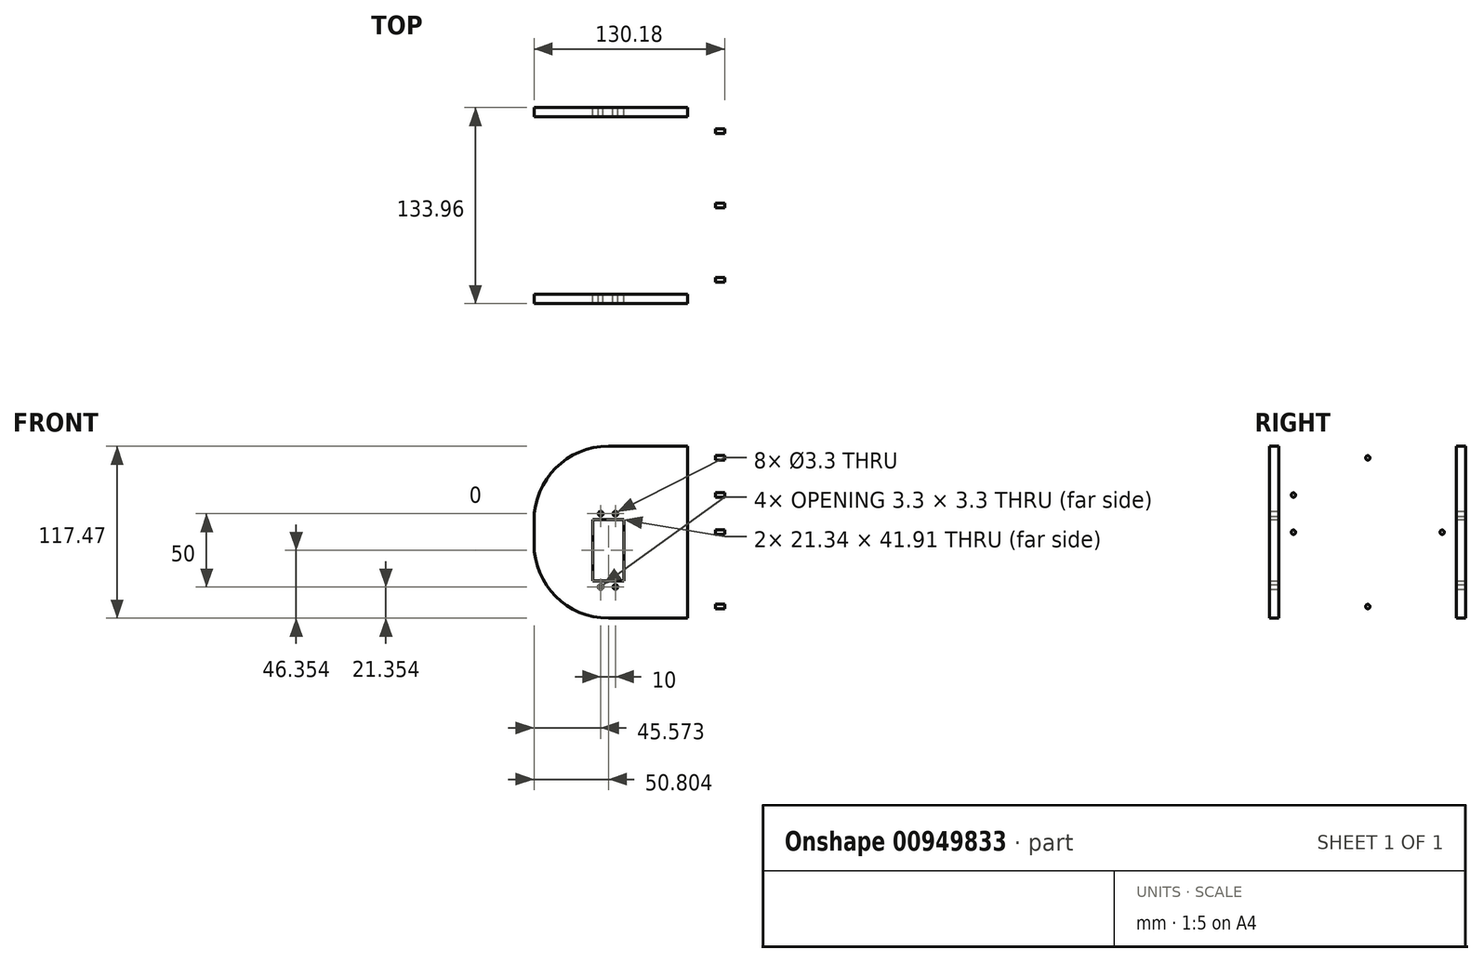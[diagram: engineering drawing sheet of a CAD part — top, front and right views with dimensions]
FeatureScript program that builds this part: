
annotation { "Feature Type Name" : "Feature", "Feature Type Description" : "" }
export const myFeature = defineFeature(function(context is Context, id is Id, definition is map)
    precondition{}
    {
        {
            var Q0;
            Q0=qCreatedBy(makeId("Front.planeOp"),FACE);
            var sketch = newSketch(context, id + "F0", { "sketchPlane" : qUnion([Q0])});
            skLineSegment(sketch, "E0.bottom", {"start": v(-34.7, 53.19) * mm, "end": v(-13.36, 53.19) * mm});
            skLineSegment(sketch, "E0.top", {"start": v(-34.7, 11.28) * mm, "end": v(-13.36, 11.28) * mm});
            skLineSegment(sketch, "E0.left", {"start": v(-34.7, 53.19) * mm, "end": v(-34.7, 11.28) * mm});
            skLineSegment(sketch, "E0.right", {"start": v(-13.36, 53.19) * mm, "end": v(-13.36, 11.28) * mm});
            skCircle(sketch, "E1", {"center": v(-29.26, 7.23) * mm, "radius": 1.65 * mm});
            skCircle(sketch, "E2", {"center": v(-19.26, 7.23) * mm, "radius": 1.65 * mm});
            skCircle(sketch, "E3.MirrorC", {"center": v(-29.26, 57.23) * mm, "radius": 1.65 * mm});
            skCircle(sketch, "E4.MirrorC", {"center": v(-19.26, 57.23) * mm, "radius": 1.65 * mm});
            skLineSegment(sketch, "E5", {"start": v(-24.03, 11.28) * mm, "end": v(-24.03, -14.12) * mm});
            skLineSegment(sketch, "E6", {"start": v(-24.03, -14.12) * mm, "end": v(55.35, -14.12) * mm});
            skLineSegment(sketch, "E7", {"start": v(-24.03, 11.28) * mm, "end": v(-24.03, 103.35) * mm});
            skLineSegment(sketch, "E8", {"start": v(55.35, -14.12) * mm, "end": v(55.35, 103.35) * mm});
            skLineSegment(sketch, "E9", {"start": v(55.35, 103.35) * mm, "end": v(-24.03, 103.35) * mm});
            skLineSegment(sketch, "E10", {"start": v(-24.03, -14.12) * mm, "end": v(-74.83, -14.12) * mm});
            skLineSegment(sketch, "E11", {"start": v(-74.83, -14.12) * mm, "end": v(-74.83, 103.35) * mm});
            skLineSegment(sketch, "E12", {"start": v(-74.83, 103.35) * mm, "end": v(-24.03, 103.35) * mm});
            skSolve(sketch);
        }
        {
            var Q0;
            {var subQ0=sQuery(id+"F0.wireOp",EDGE,"E0.left");Q0=makeQuery(id+"F0.imprint","IMPRINT",FACE,{"disambiguationData":[TD([[makeQuery(id+"F0.imprint","IMPRINT",EDGE,{"derivedFrom":subQ0}),-1.0]])]});}
            var Q1;
            {var subQ0=sQuery(id+"F0.wireOp",EDGE,"E0.right");Q1=makeQuery(id+"F0.imprint","IMPRINT",FACE,{"disambiguationData":[TD([[makeQuery(id+"F0.imprint","IMPRINT",EDGE,{"derivedFrom":subQ0}),1.0]])]});}
            extrude(context, id + "F1", {"entities" : qUnion([Q0, Q1]), "depth" : 133.96 * mm, "offsetDistance" : 25.4 * mm});
        }
        {
            var Q0;
            Q0=makeQuery(id+"F1.opExtrude","SWEPT_FACE",FACE,{"disambiguationData":[OSD([sQuery(id+"F0.wireOp",EDGE,"E11")])]});
            var sketch = newSketch(context, id + "F2", { "sketchPlane" : qUnion([Q0])});
            skLineSegment(sketch, "E13.bottom", {"start": v(6.35, 103.35) * mm, "end": v(127.6, 103.35) * mm});
            skLineSegment(sketch, "E13.top", {"start": v(6.35, -14.12) * mm, "end": v(127.6, -14.12) * mm});
            skLineSegment(sketch, "E13.left", {"start": v(6.35, 103.35) * mm, "end": v(6.35, -14.12) * mm});
            skLineSegment(sketch, "E13.right", {"start": v(127.6, 103.35) * mm, "end": v(127.6, -14.12) * mm});
            skLineSegment(sketch, "E14.bottom", {"start": v(127.6, -14.12) * mm, "end": v(111.67, -14.12) * mm});
            skSolve(sketch);
        }
        {
            var Q0;
            Q0=makeQuery(id+"F2.imprint","IMPRINT",FACE,{"disambiguationData":[TD([[makeQuery(id+"F2.imprint","IMPRINT",EDGE,{"derivedFrom":sQuery(id+"F2.wireOp",EDGE,"E13.bottom")}),1.0]])]});
            extrude(context, id + "F3", {"entities" : qUnion([Q0]), "operationType" : NewBodyOperationType.REMOVE, "oppositeDirection" : true, "depth" : 123.82 * mm, "offsetDistance" : 25.4 * mm});
        }
        {
            var Q0;
            {var subQ0=sQuery(id+"F0.wireOp",EDGE,"E11");var subQ1=sQuery(id+"F0.wireOp",EDGE,"E10");Q0=makeQuery(id+"F3.boolean.opBoolean","SPLIT",EDGE,{"disambiguationData":[TD([makeQuery(id+"F3.opExtrude","SWEPT_FACE",FACE,{"disambiguationData":[OSD([sQuery(id+"F2.wireOp",EDGE,"E13.right")])]})])],"derivedFrom":makeQuery(id+"F1.opExtrude","SWEPT_EDGE",EDGE,{"disambiguationData":[OSD([subQ1,subQ0])]})});}
            var Q1;
            {var subQ0=sQuery(id+"F0.wireOp",EDGE,"E12");var subQ1=sQuery(id+"F0.wireOp",EDGE,"E11");Q1=makeQuery(id+"F3.boolean.opBoolean","SPLIT",EDGE,{"disambiguationData":[TD([makeQuery(id+"F3.opExtrude","SWEPT_FACE",FACE,{"disambiguationData":[OSD([sQuery(id+"F2.wireOp",EDGE,"E13.right")])]})])],"derivedFrom":makeQuery(id+"F1.opExtrude","SWEPT_EDGE",EDGE,{"disambiguationData":[OSD([subQ1,subQ0])]})});}
            var Q2;
            {var subQ0=sQuery(id+"F0.wireOp",EDGE,"E11");var subQ1=sQuery(id+"F0.wireOp",EDGE,"E10");Q2=makeQuery(id+"F3.boolean.opBoolean","SPLIT",EDGE,{"disambiguationData":[TD([makeQuery(id+"F3.opExtrude","SWEPT_FACE",FACE,{"disambiguationData":[OSD([sQuery(id+"F2.wireOp",EDGE,"E13.left")])]})])],"derivedFrom":makeQuery(id+"F1.opExtrude","SWEPT_EDGE",EDGE,{"disambiguationData":[OSD([subQ1,subQ0])]})});}
            var Q3;
            {var subQ0=sQuery(id+"F0.wireOp",EDGE,"E12");var subQ1=sQuery(id+"F0.wireOp",EDGE,"E11");Q3=makeQuery(id+"F3.boolean.opBoolean","SPLIT",EDGE,{"disambiguationData":[TD([makeQuery(id+"F3.opExtrude","SWEPT_FACE",FACE,{"disambiguationData":[OSD([sQuery(id+"F2.wireOp",EDGE,"E13.left")])]})])],"derivedFrom":makeQuery(id+"F1.opExtrude","SWEPT_EDGE",EDGE,{"disambiguationData":[OSD([subQ1,subQ0])]})});}
            fillet(context, id + "F4", {"entities" : qUnion([Q0, Q1, Q2, Q3]), "radius" : 50.8 * mm, "tangentPropagation" : true, "allowEdgeOverflow" : false});
        }
        {
            var Q0;
            Q0=makeQuery(id+"F1.opExtrude","SWEPT_FACE",FACE,{"disambiguationData":[OSD([sQuery(id+"F0.wireOp",EDGE,"E8")])]});
            var sketch = newSketch(context, id + "F5", { "sketchPlane" : qUnion([Q0])});
            skLineSegment(sketch, "E15.bottom", {"start": v(-16.18, 95.42) * mm, "end": v(-117.78, 95.42) * mm});
            skLineSegment(sketch, "E15.top", {"start": v(-16.18, -6.18) * mm, "end": v(-117.78, -6.18) * mm});
            skLineSegment(sketch, "E15.left", {"start": v(-16.18, 95.42) * mm, "end": v(-16.18, -6.18) * mm});
            skLineSegment(sketch, "E15.right", {"start": v(-117.78, 95.42) * mm, "end": v(-117.78, -6.18) * mm});
            skPoint(sketch, "E15.middle", {"position": v(-66.98, 44.62) * mm});
            skPoint(sketch, "E15.middle.positionSnap0", {"position": v(0, 44.62) * mm});
            skPoint(sketch, "E15.middle.positionSnap1", {"position": v(-66.98, -14.12) * mm});
            skPoint(sketch, "E15.centerSnap0", {"position": v(0, 44.62) * mm});
            skPoint(sketch, "E15.centerSnap1", {"position": v(-66.98, -14.12) * mm});
            skCircle(sketch, "E16", {"center": v(-117.78, 95.42) * mm, "radius": 1.5 * mm});
            skCircle(sketch, "E17.0.1.0", {"center": v(-117.78, 70.02) * mm, "radius": 1.5 * mm});
            skCircle(sketch, "E17.0.2.0", {"center": v(-117.78, 44.62) * mm, "radius": 1.5 * mm});
            skCircle(sketch, "E17.0.3.0", {"center": v(-117.78, 19.22) * mm, "radius": 1.5 * mm});
            skCircle(sketch, "E17.0.4.0", {"center": v(-117.78, -6.18) * mm, "radius": 1.5 * mm});
            skCircle(sketch, "E17.1.0.0", {"center": v(-92.38, 95.42) * mm, "radius": 1.5 * mm});
            skCircle(sketch, "E17.1.1.0", {"center": v(-92.38, 70.02) * mm, "radius": 1.5 * mm});
            skCircle(sketch, "E17.1.2.0", {"center": v(-92.38, 44.62) * mm, "radius": 1.5 * mm});
            skCircle(sketch, "E17.1.3.0", {"center": v(-92.38, 19.22) * mm, "radius": 1.5 * mm});
            skCircle(sketch, "E17.1.4.0", {"center": v(-92.38, -6.18) * mm, "radius": 1.5 * mm});
            skCircle(sketch, "E17.2.0.0", {"center": v(-66.98, 95.42) * mm, "radius": 1.5 * mm});
            skCircle(sketch, "E17.2.1.0", {"center": v(-66.98, 70.02) * mm, "radius": 1.5 * mm});
            skCircle(sketch, "E17.2.2.0", {"center": v(-66.98, 44.62) * mm, "radius": 1.5 * mm});
            skCircle(sketch, "E17.2.3.0", {"center": v(-66.98, 19.22) * mm, "radius": 1.5 * mm});
            skCircle(sketch, "E17.2.4.0", {"center": v(-66.98, -6.18) * mm, "radius": 1.5 * mm});
            skCircle(sketch, "E17.3.0.0", {"center": v(-41.58, 95.42) * mm, "radius": 1.5 * mm});
            skCircle(sketch, "E17.3.1.0", {"center": v(-41.58, 70.02) * mm, "radius": 1.5 * mm});
            skCircle(sketch, "E17.3.2.0", {"center": v(-41.58, 44.62) * mm, "radius": 1.5 * mm});
            skCircle(sketch, "E17.3.3.0", {"center": v(-41.58, 19.22) * mm, "radius": 1.5 * mm});
            skCircle(sketch, "E17.3.4.0", {"center": v(-41.58, -6.18) * mm, "radius": 1.5 * mm});
            skCircle(sketch, "E17.4.0.0", {"center": v(-16.18, 95.42) * mm, "radius": 1.5 * mm});
            skCircle(sketch, "E17.4.1.0", {"center": v(-16.18, 70.02) * mm, "radius": 1.5 * mm});
            skCircle(sketch, "E17.4.2.0", {"center": v(-16.18, 44.62) * mm, "radius": 1.5 * mm});
            skCircle(sketch, "E17.4.3.0", {"center": v(-16.18, 19.22) * mm, "radius": 1.5 * mm});
            skCircle(sketch, "E17.4.4.0", {"center": v(-16.18, -6.18) * mm, "radius": 1.5 * mm});
            skLineSegment(sketch, "E17.direction1", {"start": v(-117.78, 95.42) * mm, "end": v(-92.38, 95.42) * mm, "construction": true});
            skLineSegment(sketch, "E17.direction2", {"start": v(-117.78, 95.42) * mm, "end": v(-117.78, 70.02) * mm, "construction": true});
            skSolve(sketch);
        }
        {
            var Q0;
            {var subQ0=sQuery(id+"F5.wireOp",EDGE,"E17.0.2.0");var subQ1=sQuery(id+"F5.wireOp",EDGE,"E15.right");var subQ2=makeQuery(id+"F5.imprint","INTERSECT",VERTEX,{"disambiguationData":[OD(0.0)],"derivedFrom":[subQ1,subQ0]});Q0=makeQuery(id+"F5.imprint","IMPRINT",FACE,{"disambiguationData":[TD([[makeQuery(id+"F5.imprint","IMPRINT",EDGE,{"disambiguationData":[TD([[subQ2,-1.0]])],"derivedFrom":subQ1}),1.0]])]});}
            var Q1;
            {var subQ0=sQuery(id+"F5.wireOp",EDGE,"E17.0.2.0");var subQ1=sQuery(id+"F5.wireOp",EDGE,"E15.right");var subQ2=makeQuery(id+"F5.imprint","INTERSECT",VERTEX,{"disambiguationData":[OD(0.0)],"derivedFrom":[subQ1,subQ0]});Q1=makeQuery(id+"F5.imprint","IMPRINT",FACE,{"disambiguationData":[TD([[makeQuery(id+"F5.imprint","IMPRINT",EDGE,{"disambiguationData":[TD([[subQ2,-1.0]])],"derivedFrom":subQ1}),-1.0]])]});}
            var Q2;
            Q2=makeQuery(id+"F5.imprint","IMPRINT",FACE,{"disambiguationData":[TD([[makeQuery(id+"F5.imprint","IMPRINT",EDGE,{"derivedFrom":sQuery(id+"F5.wireOp",EDGE,"E17.1.2.0")}),1.0]])]});
            var Q3;
            Q3=makeQuery(id+"F5.imprint","IMPRINT",FACE,{"disambiguationData":[TD([[makeQuery(id+"F5.imprint","IMPRINT",EDGE,{"derivedFrom":sQuery(id+"F5.wireOp",EDGE,"E17.2.2.0")}),1.0]])]});
            var Q4;
            Q4=makeQuery(id+"F5.imprint","IMPRINT",FACE,{"disambiguationData":[TD([[makeQuery(id+"F5.imprint","IMPRINT",EDGE,{"derivedFrom":sQuery(id+"F5.wireOp",EDGE,"E17.3.2.0")}),1.0]])]});
            var Q5;
            {var subQ0=sQuery(id+"F5.wireOp",EDGE,"E17.4.2.0");var subQ1=sQuery(id+"F5.wireOp",EDGE,"E15.left");var subQ2=makeQuery(id+"F5.imprint","INTERSECT",VERTEX,{"disambiguationData":[OD(0.0)],"derivedFrom":[subQ1,subQ0]});Q5=makeQuery(id+"F5.imprint","IMPRINT",FACE,{"disambiguationData":[TD([[makeQuery(id+"F5.imprint","IMPRINT",EDGE,{"disambiguationData":[TD([[subQ2,-1.0]])],"derivedFrom":subQ1}),-1.0]])]});}
            var Q6;
            {var subQ0=sQuery(id+"F5.wireOp",EDGE,"E17.4.2.0");var subQ1=sQuery(id+"F5.wireOp",EDGE,"E15.left");var subQ2=makeQuery(id+"F5.imprint","INTERSECT",VERTEX,{"disambiguationData":[OD(0.0)],"derivedFrom":[subQ1,subQ0]});Q6=makeQuery(id+"F5.imprint","IMPRINT",FACE,{"disambiguationData":[TD([[makeQuery(id+"F5.imprint","IMPRINT",EDGE,{"disambiguationData":[TD([[subQ2,-1.0]])],"derivedFrom":subQ1}),1.0]])]});}
            var Q7;
            {var subQ0=sQuery(id+"F5.wireOp",EDGE,"E17.4.3.0");var subQ1=sQuery(id+"F5.wireOp",EDGE,"E15.left");var subQ2=makeQuery(id+"F5.imprint","INTERSECT",VERTEX,{"disambiguationData":[OD(0.0)],"derivedFrom":[subQ1,subQ0]});Q7=makeQuery(id+"F5.imprint","IMPRINT",FACE,{"disambiguationData":[TD([[makeQuery(id+"F5.imprint","IMPRINT",EDGE,{"disambiguationData":[TD([[subQ2,-1.0]])],"derivedFrom":subQ1}),-1.0]])]});}
            var Q8;
            {var subQ0=sQuery(id+"F5.wireOp",EDGE,"E17.4.3.0");var subQ1=sQuery(id+"F5.wireOp",EDGE,"E15.left");var subQ2=makeQuery(id+"F5.imprint","INTERSECT",VERTEX,{"disambiguationData":[OD(0.0)],"derivedFrom":[subQ1,subQ0]});Q8=makeQuery(id+"F5.imprint","IMPRINT",FACE,{"disambiguationData":[TD([[makeQuery(id+"F5.imprint","IMPRINT",EDGE,{"disambiguationData":[TD([[subQ2,-1.0]])],"derivedFrom":subQ1}),1.0]])]});}
            var Q9;
            Q9=makeQuery(id+"F5.imprint","IMPRINT",FACE,{"disambiguationData":[TD([[makeQuery(id+"F5.imprint","IMPRINT",EDGE,{"derivedFrom":sQuery(id+"F5.wireOp",EDGE,"E17.3.3.0")}),1.0]])]});
            var Q10;
            Q10=makeQuery(id+"F5.imprint","IMPRINT",FACE,{"disambiguationData":[TD([[makeQuery(id+"F5.imprint","IMPRINT",EDGE,{"derivedFrom":sQuery(id+"F5.wireOp",EDGE,"E17.2.3.0")}),1.0]])]});
            var Q11;
            Q11=makeQuery(id+"F5.imprint","IMPRINT",FACE,{"disambiguationData":[TD([[makeQuery(id+"F5.imprint","IMPRINT",EDGE,{"derivedFrom":sQuery(id+"F5.wireOp",EDGE,"E17.1.3.0")}),1.0]])]});
            var Q12;
            {var subQ0=sQuery(id+"F5.wireOp",EDGE,"E17.0.3.0");var subQ1=sQuery(id+"F5.wireOp",EDGE,"E15.right");var subQ2=makeQuery(id+"F5.imprint","INTERSECT",VERTEX,{"disambiguationData":[OD(0.0)],"derivedFrom":[subQ1,subQ0]});Q12=makeQuery(id+"F5.imprint","IMPRINT",FACE,{"disambiguationData":[TD([[makeQuery(id+"F5.imprint","IMPRINT",EDGE,{"disambiguationData":[TD([[subQ2,-1.0]])],"derivedFrom":subQ1}),-1.0]])]});}
            var Q13;
            {var subQ0=sQuery(id+"F5.wireOp",EDGE,"E15.right");var subQ1=sQuery(id+"F5.wireOp",EDGE,"E15.top");var subQ2=makeQuery(id+"F5.imprint","INTERSECT",VERTEX,{"derivedFrom":[subQ1,subQ0]});Q13=makeQuery(id+"F5.imprint","IMPRINT",FACE,{"disambiguationData":[TD([[makeQuery(id+"F5.imprint","IMPRINT",EDGE,{"disambiguationData":[TD([[subQ2,1.0]])],"derivedFrom":subQ1}),1.0]])]});}
            var Q14;
            {var subQ0=sQuery(id+"F5.wireOp",EDGE,"E17.0.3.0");var subQ1=sQuery(id+"F5.wireOp",EDGE,"E15.right");var subQ2=makeQuery(id+"F5.imprint","INTERSECT",VERTEX,{"disambiguationData":[OD(0.0)],"derivedFrom":[subQ1,subQ0]});Q14=makeQuery(id+"F5.imprint","IMPRINT",FACE,{"disambiguationData":[TD([[makeQuery(id+"F5.imprint","IMPRINT",EDGE,{"disambiguationData":[TD([[subQ2,-1.0]])],"derivedFrom":subQ1}),1.0]])]});}
            var Q15;
            {var subQ0=sQuery(id+"F5.wireOp",EDGE,"E17.1.4.0");var subQ1=sQuery(id+"F5.wireOp",EDGE,"E15.top");var subQ2=makeQuery(id+"F5.imprint","INTERSECT",VERTEX,{"disambiguationData":[OD(0.0)],"derivedFrom":[subQ1,subQ0]});Q15=makeQuery(id+"F5.imprint","IMPRINT",FACE,{"disambiguationData":[TD([[makeQuery(id+"F5.imprint","IMPRINT",EDGE,{"disambiguationData":[TD([[subQ2,-1.0]])],"derivedFrom":subQ1}),-1.0]])]});}
            var Q16;
            {var subQ0=sQuery(id+"F5.wireOp",EDGE,"E17.1.4.0");var subQ1=sQuery(id+"F5.wireOp",EDGE,"E15.top");var subQ2=makeQuery(id+"F5.imprint","INTERSECT",VERTEX,{"disambiguationData":[OD(0.0)],"derivedFrom":[subQ1,subQ0]});Q16=makeQuery(id+"F5.imprint","IMPRINT",FACE,{"disambiguationData":[TD([[makeQuery(id+"F5.imprint","IMPRINT",EDGE,{"disambiguationData":[TD([[subQ2,-1.0]])],"derivedFrom":subQ1}),1.0]])]});}
            var Q17;
            {var subQ0=sQuery(id+"F5.wireOp",EDGE,"E17.2.4.0");var subQ1=sQuery(id+"F5.wireOp",EDGE,"E15.top");var subQ2=makeQuery(id+"F5.imprint","INTERSECT",VERTEX,{"disambiguationData":[OD(0.0)],"derivedFrom":[subQ1,subQ0]});Q17=makeQuery(id+"F5.imprint","IMPRINT",FACE,{"disambiguationData":[TD([[makeQuery(id+"F5.imprint","IMPRINT",EDGE,{"disambiguationData":[TD([[subQ2,-1.0]])],"derivedFrom":subQ1}),-1.0]])]});}
            var Q18;
            {var subQ0=sQuery(id+"F5.wireOp",EDGE,"E17.2.4.0");var subQ1=sQuery(id+"F5.wireOp",EDGE,"E15.top");var subQ2=makeQuery(id+"F5.imprint","INTERSECT",VERTEX,{"disambiguationData":[OD(0.0)],"derivedFrom":[subQ1,subQ0]});Q18=makeQuery(id+"F5.imprint","IMPRINT",FACE,{"disambiguationData":[TD([[makeQuery(id+"F5.imprint","IMPRINT",EDGE,{"disambiguationData":[TD([[subQ2,-1.0]])],"derivedFrom":subQ1}),1.0]])]});}
            var Q19;
            {var subQ0=sQuery(id+"F5.wireOp",EDGE,"E17.3.4.0");var subQ1=sQuery(id+"F5.wireOp",EDGE,"E15.top");var subQ2=makeQuery(id+"F5.imprint","INTERSECT",VERTEX,{"disambiguationData":[OD(0.0)],"derivedFrom":[subQ1,subQ0]});Q19=makeQuery(id+"F5.imprint","IMPRINT",FACE,{"disambiguationData":[TD([[makeQuery(id+"F5.imprint","IMPRINT",EDGE,{"disambiguationData":[TD([[subQ2,-1.0]])],"derivedFrom":subQ1}),-1.0]])]});}
            var Q20;
            {var subQ0=sQuery(id+"F5.wireOp",EDGE,"E17.3.4.0");var subQ1=sQuery(id+"F5.wireOp",EDGE,"E15.top");var subQ2=makeQuery(id+"F5.imprint","INTERSECT",VERTEX,{"disambiguationData":[OD(0.0)],"derivedFrom":[subQ1,subQ0]});Q20=makeQuery(id+"F5.imprint","IMPRINT",FACE,{"disambiguationData":[TD([[makeQuery(id+"F5.imprint","IMPRINT",EDGE,{"disambiguationData":[TD([[subQ2,-1.0]])],"derivedFrom":subQ1}),1.0]])]});}
            var Q21;
            {var subQ0=sQuery(id+"F5.wireOp",EDGE,"E15.left");var subQ1=sQuery(id+"F5.wireOp",EDGE,"E15.top");var subQ2=makeQuery(id+"F5.imprint","INTERSECT",VERTEX,{"derivedFrom":[subQ1,subQ0]});Q21=makeQuery(id+"F5.imprint","IMPRINT",FACE,{"disambiguationData":[TD([[makeQuery(id+"F5.imprint","IMPRINT",EDGE,{"disambiguationData":[TD([[subQ2,-1.0]])],"derivedFrom":subQ1}),1.0]])]});}
            var Q22;
            {var subQ0=sQuery(id+"F5.wireOp",EDGE,"E15.left");var subQ1=sQuery(id+"F5.wireOp",EDGE,"E15.top");var subQ2=makeQuery(id+"F5.imprint","INTERSECT",VERTEX,{"derivedFrom":[subQ1,subQ0]});Q22=makeQuery(id+"F5.imprint","IMPRINT",FACE,{"disambiguationData":[TD([[makeQuery(id+"F5.imprint","IMPRINT",EDGE,{"disambiguationData":[TD([[subQ2,-1.0]])],"derivedFrom":subQ1}),-1.0]])]});}
            var Q23;
            {var subQ0=sQuery(id+"F5.wireOp",EDGE,"E15.right");var subQ1=sQuery(id+"F5.wireOp",EDGE,"E15.top");var subQ2=makeQuery(id+"F5.imprint","INTERSECT",VERTEX,{"derivedFrom":[subQ1,subQ0]});Q23=makeQuery(id+"F5.imprint","IMPRINT",FACE,{"disambiguationData":[TD([[makeQuery(id+"F5.imprint","IMPRINT",EDGE,{"disambiguationData":[TD([[subQ2,1.0]])],"derivedFrom":subQ1}),-1.0]])]});}
            var Q24;
            {var subQ0=sQuery(id+"F5.wireOp",EDGE,"E17.0.1.0");var subQ1=sQuery(id+"F5.wireOp",EDGE,"E15.right");var subQ2=makeQuery(id+"F5.imprint","INTERSECT",VERTEX,{"disambiguationData":[OD(0.0)],"derivedFrom":[subQ1,subQ0]});Q24=makeQuery(id+"F5.imprint","IMPRINT",FACE,{"disambiguationData":[TD([[makeQuery(id+"F5.imprint","IMPRINT",EDGE,{"disambiguationData":[TD([[subQ2,-1.0]])],"derivedFrom":subQ1}),1.0]])]});}
            var Q25;
            {var subQ0=sQuery(id+"F5.wireOp",EDGE,"E17.0.1.0");var subQ1=sQuery(id+"F5.wireOp",EDGE,"E15.right");var subQ2=makeQuery(id+"F5.imprint","INTERSECT",VERTEX,{"disambiguationData":[OD(0.0)],"derivedFrom":[subQ1,subQ0]});Q25=makeQuery(id+"F5.imprint","IMPRINT",FACE,{"disambiguationData":[TD([[makeQuery(id+"F5.imprint","IMPRINT",EDGE,{"disambiguationData":[TD([[subQ2,-1.0]])],"derivedFrom":subQ1}),-1.0]])]});}
            var Q26;
            Q26=makeQuery(id+"F5.imprint","IMPRINT",FACE,{"disambiguationData":[TD([[makeQuery(id+"F5.imprint","IMPRINT",EDGE,{"derivedFrom":sQuery(id+"F5.wireOp",EDGE,"E17.1.1.0")}),1.0]])]});
            var Q27;
            Q27=makeQuery(id+"F5.imprint","IMPRINT",FACE,{"disambiguationData":[TD([[makeQuery(id+"F5.imprint","IMPRINT",EDGE,{"derivedFrom":sQuery(id+"F5.wireOp",EDGE,"E17.2.1.0")}),1.0]])]});
            var Q28;
            Q28=makeQuery(id+"F5.imprint","IMPRINT",FACE,{"disambiguationData":[TD([[makeQuery(id+"F5.imprint","IMPRINT",EDGE,{"derivedFrom":sQuery(id+"F5.wireOp",EDGE,"E17.3.1.0")}),1.0]])]});
            var Q29;
            {var subQ0=sQuery(id+"F5.wireOp",EDGE,"E17.4.1.0");var subQ1=sQuery(id+"F5.wireOp",EDGE,"E15.left");var subQ2=makeQuery(id+"F5.imprint","INTERSECT",VERTEX,{"disambiguationData":[OD(0.0)],"derivedFrom":[subQ1,subQ0]});Q29=makeQuery(id+"F5.imprint","IMPRINT",FACE,{"disambiguationData":[TD([[makeQuery(id+"F5.imprint","IMPRINT",EDGE,{"disambiguationData":[TD([[subQ2,-1.0]])],"derivedFrom":subQ1}),1.0]])]});}
            var Q30;
            {var subQ0=sQuery(id+"F5.wireOp",EDGE,"E17.4.1.0");var subQ1=sQuery(id+"F5.wireOp",EDGE,"E15.left");var subQ2=makeQuery(id+"F5.imprint","INTERSECT",VERTEX,{"disambiguationData":[OD(0.0)],"derivedFrom":[subQ1,subQ0]});Q30=makeQuery(id+"F5.imprint","IMPRINT",FACE,{"disambiguationData":[TD([[makeQuery(id+"F5.imprint","IMPRINT",EDGE,{"disambiguationData":[TD([[subQ2,-1.0]])],"derivedFrom":subQ1}),-1.0]])]});}
            var Q31;
            {var subQ0=sQuery(id+"F5.wireOp",EDGE,"E15.left");var subQ1=sQuery(id+"F5.wireOp",EDGE,"E15.bottom");var subQ2=makeQuery(id+"F5.imprint","INTERSECT",VERTEX,{"derivedFrom":[subQ1,subQ0]});Q31=makeQuery(id+"F5.imprint","IMPRINT",FACE,{"disambiguationData":[TD([[makeQuery(id+"F5.imprint","IMPRINT",EDGE,{"disambiguationData":[TD([[subQ2,-1.0]])],"derivedFrom":subQ1}),-1.0]])]});}
            var Q32;
            {var subQ0=sQuery(id+"F5.wireOp",EDGE,"E15.left");var subQ1=sQuery(id+"F5.wireOp",EDGE,"E15.bottom");var subQ2=makeQuery(id+"F5.imprint","INTERSECT",VERTEX,{"derivedFrom":[subQ1,subQ0]});Q32=makeQuery(id+"F5.imprint","IMPRINT",FACE,{"disambiguationData":[TD([[makeQuery(id+"F5.imprint","IMPRINT",EDGE,{"disambiguationData":[TD([[subQ2,-1.0]])],"derivedFrom":subQ1}),1.0]])]});}
            var Q33;
            {var subQ0=sQuery(id+"F5.wireOp",EDGE,"E17.3.0.0");var subQ1=sQuery(id+"F5.wireOp",EDGE,"E15.bottom");var subQ2=makeQuery(id+"F5.imprint","INTERSECT",VERTEX,{"disambiguationData":[OD(0.0)],"derivedFrom":[subQ1,subQ0]});Q33=makeQuery(id+"F5.imprint","IMPRINT",FACE,{"disambiguationData":[TD([[makeQuery(id+"F5.imprint","IMPRINT",EDGE,{"disambiguationData":[TD([[subQ2,-1.0]])],"derivedFrom":subQ1}),-1.0]])]});}
            var Q34;
            {var subQ0=sQuery(id+"F5.wireOp",EDGE,"E17.3.0.0");var subQ1=sQuery(id+"F5.wireOp",EDGE,"E15.bottom");var subQ2=makeQuery(id+"F5.imprint","INTERSECT",VERTEX,{"disambiguationData":[OD(0.0)],"derivedFrom":[subQ1,subQ0]});Q34=makeQuery(id+"F5.imprint","IMPRINT",FACE,{"disambiguationData":[TD([[makeQuery(id+"F5.imprint","IMPRINT",EDGE,{"disambiguationData":[TD([[subQ2,-1.0]])],"derivedFrom":subQ1}),1.0]])]});}
            var Q35;
            {var subQ0=sQuery(id+"F5.wireOp",EDGE,"E17.2.0.0");var subQ1=sQuery(id+"F5.wireOp",EDGE,"E15.bottom");var subQ2=makeQuery(id+"F5.imprint","INTERSECT",VERTEX,{"disambiguationData":[OD(0.0)],"derivedFrom":[subQ1,subQ0]});Q35=makeQuery(id+"F5.imprint","IMPRINT",FACE,{"disambiguationData":[TD([[makeQuery(id+"F5.imprint","IMPRINT",EDGE,{"disambiguationData":[TD([[subQ2,-1.0]])],"derivedFrom":subQ1}),1.0]])]});}
            var Q36;
            {var subQ0=sQuery(id+"F5.wireOp",EDGE,"E17.2.0.0");var subQ1=sQuery(id+"F5.wireOp",EDGE,"E15.bottom");var subQ2=makeQuery(id+"F5.imprint","INTERSECT",VERTEX,{"disambiguationData":[OD(0.0)],"derivedFrom":[subQ1,subQ0]});Q36=makeQuery(id+"F5.imprint","IMPRINT",FACE,{"disambiguationData":[TD([[makeQuery(id+"F5.imprint","IMPRINT",EDGE,{"disambiguationData":[TD([[subQ2,-1.0]])],"derivedFrom":subQ1}),-1.0]])]});}
            var Q37;
            {var subQ0=sQuery(id+"F5.wireOp",EDGE,"E17.1.0.0");var subQ1=sQuery(id+"F5.wireOp",EDGE,"E15.bottom");var subQ2=makeQuery(id+"F5.imprint","INTERSECT",VERTEX,{"disambiguationData":[OD(0.0)],"derivedFrom":[subQ1,subQ0]});Q37=makeQuery(id+"F5.imprint","IMPRINT",FACE,{"disambiguationData":[TD([[makeQuery(id+"F5.imprint","IMPRINT",EDGE,{"disambiguationData":[TD([[subQ2,-1.0]])],"derivedFrom":subQ1}),-1.0]])]});}
            var Q38;
            {var subQ0=sQuery(id+"F5.wireOp",EDGE,"E15.right");var subQ1=sQuery(id+"F5.wireOp",EDGE,"E15.bottom");var subQ2=makeQuery(id+"F5.imprint","INTERSECT",VERTEX,{"derivedFrom":[subQ1,subQ0]});Q38=makeQuery(id+"F5.imprint","IMPRINT",FACE,{"disambiguationData":[TD([[makeQuery(id+"F5.imprint","IMPRINT",EDGE,{"disambiguationData":[TD([[subQ2,1.0]])],"derivedFrom":subQ1}),-1.0]])]});}
            var Q39;
            {var subQ0=sQuery(id+"F5.wireOp",EDGE,"E15.right");var subQ1=sQuery(id+"F5.wireOp",EDGE,"E15.bottom");var subQ2=makeQuery(id+"F5.imprint","INTERSECT",VERTEX,{"derivedFrom":[subQ1,subQ0]});Q39=makeQuery(id+"F5.imprint","IMPRINT",FACE,{"disambiguationData":[TD([[makeQuery(id+"F5.imprint","IMPRINT",EDGE,{"disambiguationData":[TD([[subQ2,1.0]])],"derivedFrom":subQ1}),1.0]])]});}
            var Q40;
            {var subQ0=sQuery(id+"F5.wireOp",EDGE,"E17.1.0.0");var subQ1=sQuery(id+"F5.wireOp",EDGE,"E15.bottom");var subQ2=makeQuery(id+"F5.imprint","INTERSECT",VERTEX,{"disambiguationData":[OD(0.0)],"derivedFrom":[subQ1,subQ0]});Q40=makeQuery(id+"F5.imprint","IMPRINT",FACE,{"disambiguationData":[TD([[makeQuery(id+"F5.imprint","IMPRINT",EDGE,{"disambiguationData":[TD([[subQ2,-1.0]])],"derivedFrom":subQ1}),1.0]])]});}
            extrude(context, id + "F6", {"entities" : qUnion([Q0, Q1, Q2, Q3, Q4, Q5, Q6, Q7, Q8, Q9, Q10, Q11, Q12, Q13, Q14, Q15, Q16, Q17, Q18, Q19, Q20, Q21, Q22, Q23, Q24, Q25, Q26, Q27, Q28, Q29, Q30, Q31, Q32, Q33, Q34, Q35, Q36, Q37, Q38, Q39, Q40]), "operationType" : NewBodyOperationType.REMOVE, "oppositeDirection" : true, "depth" : 25.4 * mm, "offsetDistance" : 25.4 * mm});
        }
    });
